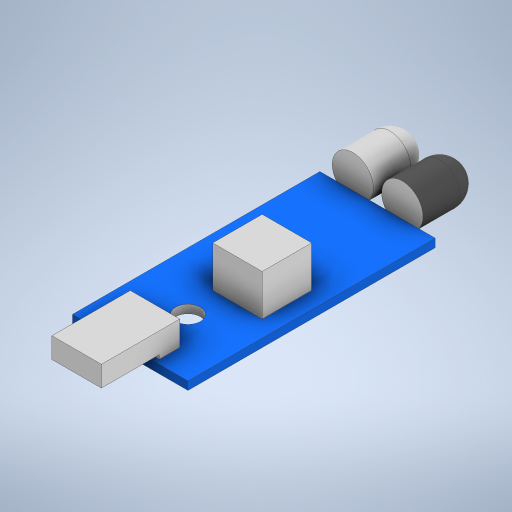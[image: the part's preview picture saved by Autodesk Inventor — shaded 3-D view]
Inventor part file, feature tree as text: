
AUTODESK INVENTOR PART (.ipt)
format: ipt  version: 2024.2 (Build 282272000, 272)  size: 334,848 bytes
history: native  units: mm
features: extrude x6, sketch x6, fillet x1
ambient origin geometry x8: Origin, YZ Plane, XZ Plane, XY Plane, X Axis, Y Axis, Z Axis, Center Point
bodies: Solid1 (feature_tree)
feature tree (13):
  extrude  "Extrusion1"  Depth=30.0mm
  extrude  "Extrusion2"  Depth=5.0mm
  fillet  "Fillet1"  Radius=5.0mm
  extrude  "Extrusion3"  Depth=4.0mm
  extrude  "Extrusion4"  Depth=7.0mm TaperAngle=0.0deg
  extrude  "Extrusion5"  Depth=6.0mm
  extrude  "Extrusion6"  Depth=2.5mm
  sketch  "Sketch1"  dims[d0=14.0mm d1=30.0mm]
  sketch  "Sketch2"  dims[d2=1.0mm d3=0.0mm d4=5.0mm d5=5.0mm]
  sketch  "Sketch3"  dims[d6=2.5mm d7=4.0mm]
  sketch  "Sketch4"  dims[d8=4.0mm d9=7.0mm d10=0.0mm]
  sketch  "Sketch5"  dims[d11=2.5mm d12=6.0mm]
  sketch  "Sketch6"  dims[d13=4.0mm d14=2.5mm d15=0.5mm d16=3.0mm d17=0.0mm d18=2.5mm d19=7.0mm d20=0.0mm d21=6.0mm d22=6.0mm d23=2.0mm d24=13.0mm d25=5.0mm d26=0.0mm d27=3.0mm d28=7.0mm d29=7.0mm d30=0.0mm d31=0.0mm]
